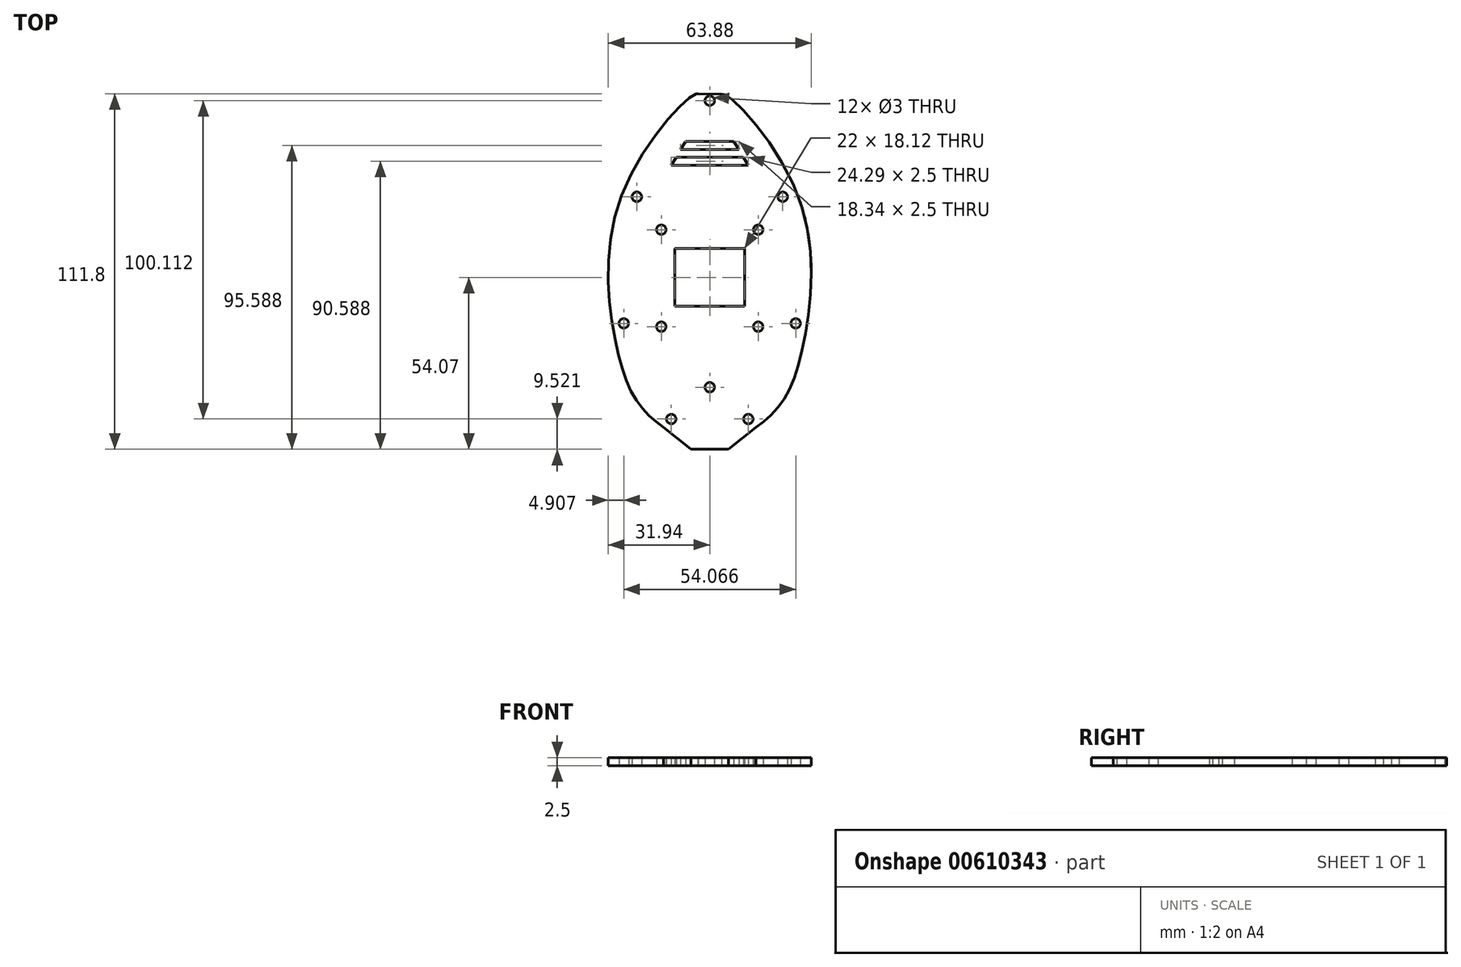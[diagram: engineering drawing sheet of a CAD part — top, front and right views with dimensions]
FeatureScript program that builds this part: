
annotation { "Feature Type Name" : "Feature", "Feature Type Description" : "" }
export const myFeature = defineFeature(function(context is Context, id is Id, definition is map)
    precondition{}
    {
        {
            var Q0;
            Q0=qCreatedBy(makeId("Top.planeOp"),FACE);
            var sketch = newSketch(context, id + "F0", { "sketchPlane" : qUnion([Q0])});
            skCircle(sketch, "E0", {"center": v(-27.03, 3.13) * mm, "radius": 1.5 * mm});
            skCircle(sketch, "E1", {"center": v(-12.12, -26.95) * mm, "radius": 1.5 * mm});
            skCircle(sketch, "E2", {"center": v(-22.94, 42.94) * mm, "radius": 1.5 * mm});
            skCircle(sketch, "E3", {"center": v(0, 73.16) * mm, "radius": 1.5 * mm});
            skCircle(sketch, "E4.MirrorC", {"center": v(22.94, 42.94) * mm, "radius": 1.5 * mm});
            skCircle(sketch, "E5.MirrorC", {"center": v(27.03, 3.13) * mm, "radius": 1.5 * mm});
            skCircle(sketch, "E6.MirrorC", {"center": v(12.12, -26.95) * mm, "radius": 1.5 * mm});
            skFitSpline(sketch, "E7", {"points": [v(-14.57, -29.55) * mm, v(-22.47, -22.07) * mm, v(-29.18, -4.58) * mm, v(-27.39, 44.23) * mm, v(-4.28, 75.27) * mm, v(-3.78, 75.26) * mm], "startDerivative": vector(-53.1, 39.59) * mm, "endDerivative": vector(-15.84, -4.32) * mm});
            skLineSegment(sketch, "E8", {"start": v(-14.57, -29.55) * mm, "end": v(-5.94, -36.47) * mm});
            skLineSegment(sketch, "E9", {"start": v(-5.94, -36.47) * mm, "end": v(0, -36.47) * mm});
            skFitSpline(sketch, "E10.MirrorCS", {"points": [v(14.57, -29.55) * mm, v(22.47, -22.07) * mm, v(29.18, -4.58) * mm, v(27.39, 44.23) * mm, v(4.28, 75.27) * mm, v(3.78, 75.26) * mm], "startDerivative": vector(53.1, 39.59) * mm, "endDerivative": vector(15.84, -4.32) * mm});
            skLineSegment(sketch, "E11.MirrorCS", {"start": v(14.57, -29.55) * mm, "end": v(5.94, -36.47) * mm});
            skLineSegment(sketch, "E12.MirrorCS", {"start": v(5.94, -36.47) * mm, "end": v(0, -36.47) * mm});
            skLineSegment(sketch, "E13", {"start": v(-3.6, 75.31) * mm, "end": v(3.78, 75.26) * mm});
            skCircle(sketch, "E14", {"center": v(-15.25, 32.58) * mm, "radius": 1.5 * mm});
            skCircle(sketch, "E15", {"center": v(-15.25, 2.08) * mm, "radius": 1.5 * mm});
            skCircle(sketch, "E16.MirrorC", {"center": v(15.25, 32.58) * mm, "radius": 1.5 * mm});
            skCircle(sketch, "E17.MirrorC", {"center": v(15.25, 2.08) * mm, "radius": 1.5 * mm});
            skCircle(sketch, "E18", {"center": v(0, -16.97) * mm, "radius": 1.5 * mm});
            skLineSegment(sketch, "E19", {"start": v(-11, 26.66) * mm, "end": v(-11, 8.54) * mm});
            skLineSegment(sketch, "E20", {"start": v(-11, 8.54) * mm, "end": v(11, 8.54) * mm});
            skLineSegment(sketch, "E21", {"start": v(11, 8.54) * mm, "end": v(11, 26.66) * mm});
            skLineSegment(sketch, "E22", {"start": v(11, 26.66) * mm, "end": v(-11, 26.66) * mm});
            skLineSegment(sketch, "E23", {"start": v(-9.17, 57.87) * mm, "end": v(-7.59, 60.37) * mm});
            skLineSegment(sketch, "E24", {"start": v(-12.14, 52.87) * mm, "end": v(-10.56, 55.37) * mm});
            skLineSegment(sketch, "E25.MirrorCS", {"start": v(9.17, 57.87) * mm, "end": v(7.59, 60.37) * mm});
            skLineSegment(sketch, "E26.MirrorCS", {"start": v(12.14, 52.87) * mm, "end": v(10.56, 55.37) * mm});
            skLineSegment(sketch, "E27", {"start": v(-7.59, 60.37) * mm, "end": v(7.59, 60.37) * mm});
            skLineSegment(sketch, "E28", {"start": v(-9.17, 57.87) * mm, "end": v(9.17, 57.87) * mm});
            skLineSegment(sketch, "E29", {"start": v(-10.56, 55.37) * mm, "end": v(10.56, 55.37) * mm});
            skLineSegment(sketch, "E30", {"start": v(-12.14, 52.87) * mm, "end": v(12.14, 52.87) * mm});
            skLineSegment(sketch, "E31", {"start": v(-4.28, 75.27) * mm, "end": v(-3.6, 75.31) * mm});
            skSolve(sketch);
        }
        {
            var Q0;
            Q0 = qSketchRegion(id + "F0", true);
            extrude(context, id + "F1", {"entities" : qUnion([Q0]), "depth" : 2.5 * mm, "offsetDistance" : 25 * mm});
        }
    });
